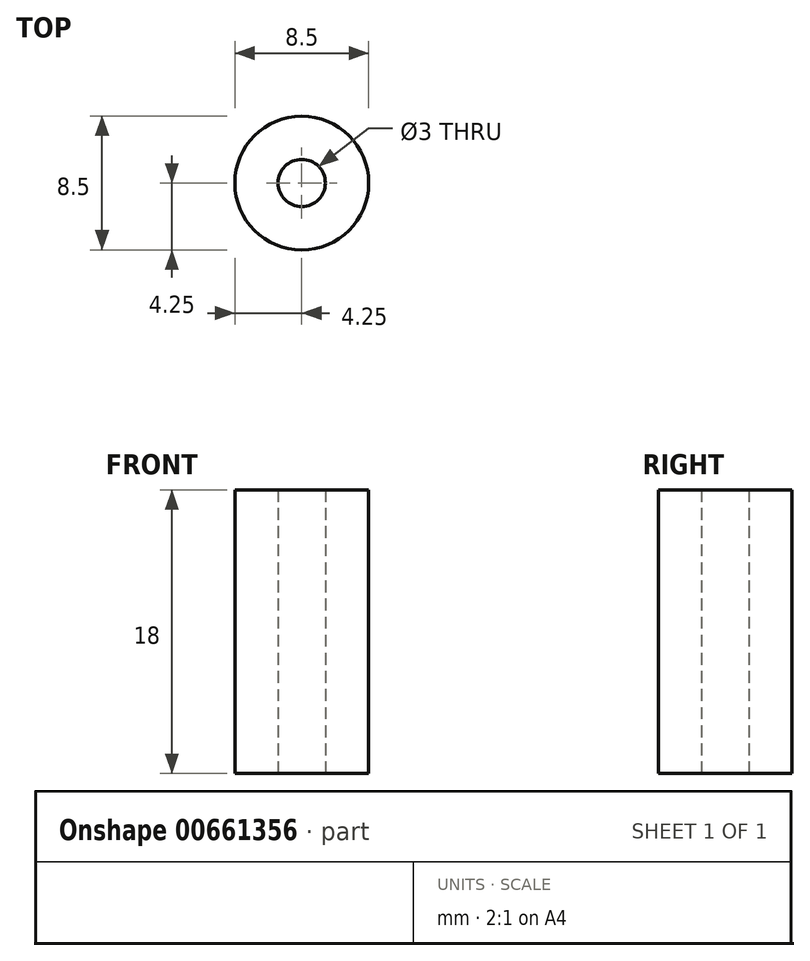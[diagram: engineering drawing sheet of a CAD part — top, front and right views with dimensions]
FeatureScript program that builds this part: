
annotation { "Feature Type Name" : "Feature", "Feature Type Description" : "" }
export const myFeature = defineFeature(function(context is Context, id is Id, definition is map)
    precondition{}
    {
        {
            var Q0;
            Q0=qCreatedBy(makeId("Front.planeOp"),FACE);
            var sketch = newSketch(context, id + "F0", { "sketchPlane" : qUnion([Q0])});
            skLineSegment(sketch, "E0", {"start": v(0, 0) * mm, "end": v(-1.5, 0) * mm, "construction": true});
            skLineSegment(sketch, "E1", {"start": v(-1.5, 0) * mm, "end": v(-4.25, 0) * mm});
            skLineSegment(sketch, "E2", {"start": v(-4.25, 0) * mm, "end": v(-4.25, 18) * mm});
            skLineSegment(sketch, "E3", {"start": v(-4.25, 18) * mm, "end": v(-1.5, 18) * mm});
            skLineSegment(sketch, "E4", {"start": v(-1.5, 18) * mm, "end": v(-1.5, 0) * mm});
            skLineSegment(sketch, "E5", {"start": v(0, 0) * mm, "end": v(0, 18) * mm, "construction": true});
            skSolve(sketch);
        }
        {
            var Q0;
            Q0 = qSketchRegion(id + "F0", true);
            var Q1;
            Q1=sQuery(id+"F0.wireOp",EDGE,"E5");
            revolve(context, id + "F1", {"entities" : qUnion([Q0]), "axis" : qUnion([Q1]), "revolveType" : RevolveType.FULL});
        }
    });
